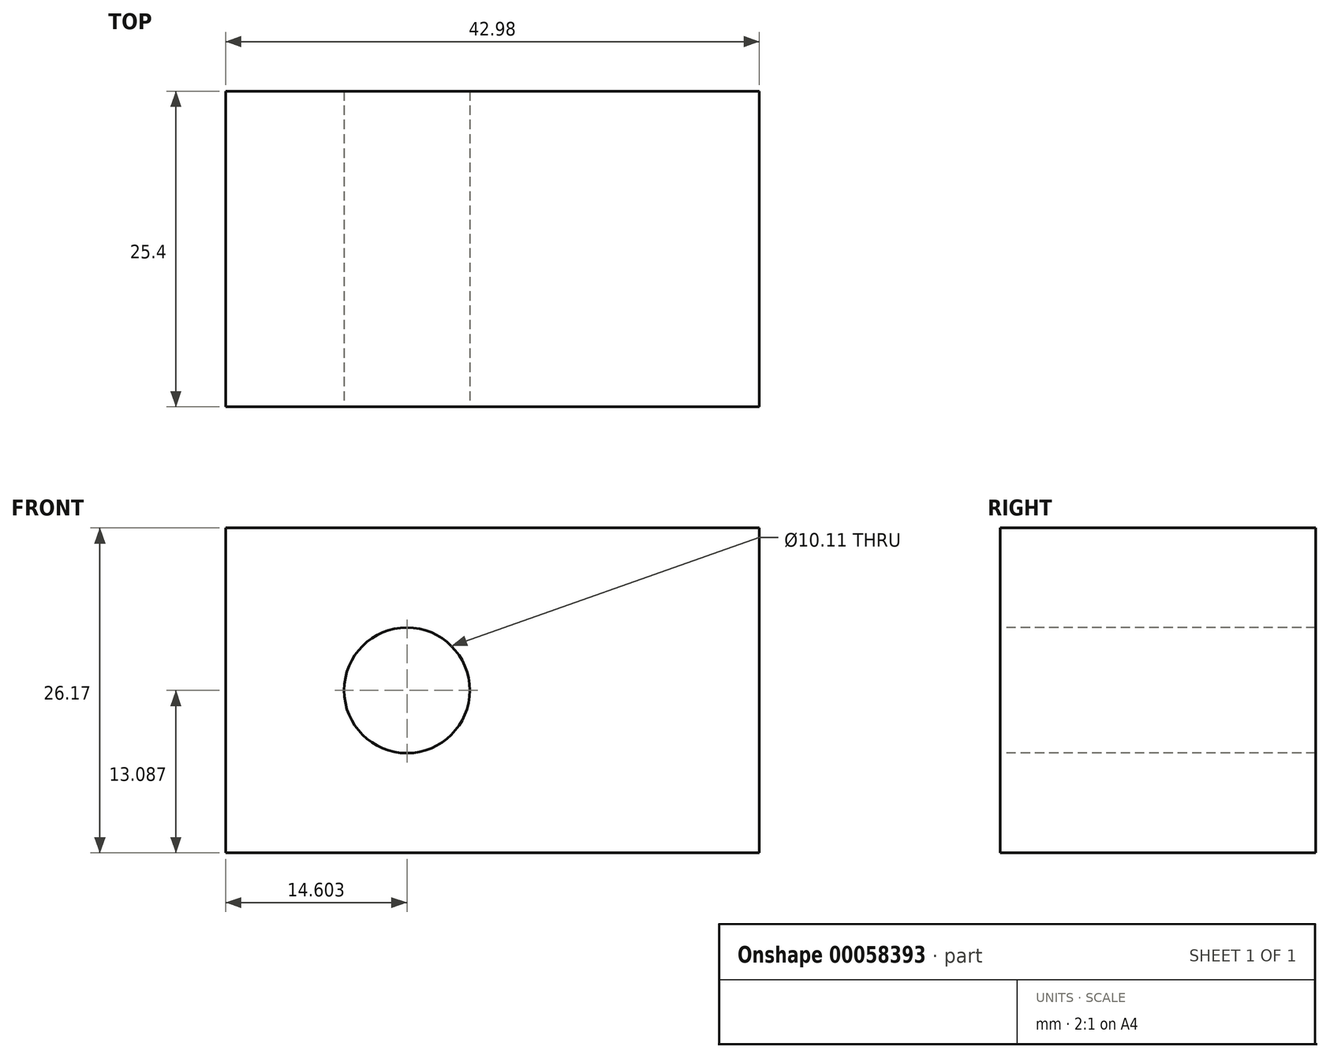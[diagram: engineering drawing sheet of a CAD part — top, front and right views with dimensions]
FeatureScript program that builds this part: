
annotation { "Feature Type Name" : "Feature", "Feature Type Description" : "" }
export const myFeature = defineFeature(function(context is Context, id is Id, definition is map)
    precondition{}
    {
        {
            var Q0;
            Q0=qCreatedBy(makeId("Front.planeOp"),FACE);
            var sketch = newSketch(context, id + "F0", { "sketchPlane" : qUnion([Q0])});
            skLineSegment(sketch, "E0.bottom", {"start": v(0, 0) * mm, "end": v(42.98, 0) * mm});
            skLineSegment(sketch, "E0.top", {"start": v(0, 26.17) * mm, "end": v(42.98, 26.17) * mm});
            skLineSegment(sketch, "E0.left", {"start": v(0, 0) * mm, "end": v(0, 26.17) * mm});
            skLineSegment(sketch, "E0.right", {"start": v(42.98, 0) * mm, "end": v(42.98, 26.17) * mm});
            skSolve(sketch);
        }
        {
            var Q0;
            Q0 = qSketchRegion(id + "F0", true);
            extrude(context, id + "F1", {"entities" : qUnion([Q0]), "oppositeDirection" : true, "depth" : 25.4 * mm});
        }
        {
            var Q0;
            Q0=makeQuery(id+"F1.opExtrude","CAP_FACE",FACE,{"disambiguationData":[OSD([sQuery(id+"F0.wireOp",EDGE,"E0.bottom"),sQuery(id+"F0.wireOp",EDGE,"E0.top"),sQuery(id+"F0.wireOp",EDGE,"E0.left"),sQuery(id+"F0.wireOp",EDGE,"E0.right")])],"isStart":true});
            var sketch = newSketch(context, id + "F2", { "sketchPlane" : qUnion([Q0])});
            skCircle(sketch, "E1", {"center": v(14.6, 13.09) * mm, "radius": 5.06 * mm});
            skPoint(sketch, "E1.centerSnap0", {"position": v(0, 13.09) * mm});
            skSolve(sketch);
        }
        {
            var Q0;
            Q0 = qSketchRegion(id + "F2", true);
            extrude(context, id + "F3", {"entities" : qUnion([Q0]), "operationType" : NewBodyOperationType.REMOVE, "endBound" : BoundingType.THROUGH_ALL, "oppositeDirection" : true, "depth" : 25.4 * mm});
        }
        {
            var Q0;
            Q0=qCreatedBy(makeId("Front.planeOp"),FACE);
            var sketch = newSketch(context, id + "F4", { "sketchPlane" : qUnion([Q0])});
            skCircle(sketch, "E2", {"center": v(-63.84, 32.47) * mm, "radius": 6.68 * mm});
            skSolve(sketch);
        }
        {
            var Q0;
            Q0=sQuery(id+"F4.wireOp",EDGE,"E2");
            extrude(context, id + "F5", {"bodyType" : ToolBodyType.SURFACE, "surfaceEntities" : qUnion([Q0]), "oppositeDirection" : true, "depth" : 50.8 * mm});
        }
    });
